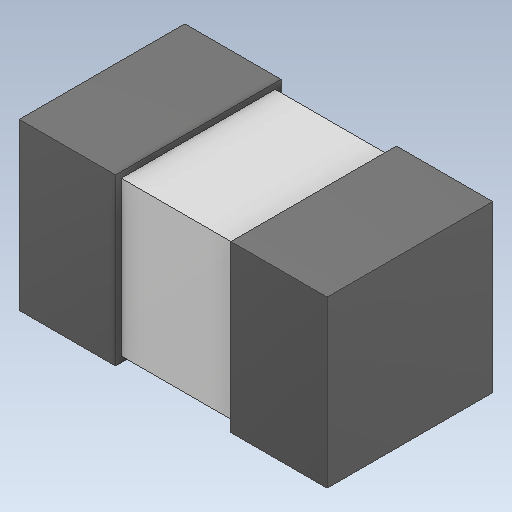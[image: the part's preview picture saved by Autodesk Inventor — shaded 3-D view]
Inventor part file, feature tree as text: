
AUTODESK INVENTOR PART (.ipt)
format: ipt  version: 2020 (Build 240168000, 168)  size: 102,912 bytes
history: native  units: mm
features: other x1, extrude x1
ambient origin geometry x8: Origin, YZ Plane, XZ Plane, XY Plane, X Axis, Y Axis, Z Axis, Center Point
bodies: Body1 (feature_tree)
feature tree (2):
  other  "Твердое тело1"
  extrude  "Extrude2"  [1 undecoded]
note: 1 required parameter value undecoded (feature->parameter linkage not recoverable at this tier; creation-order binding heuristic only, values carry confidence <= 0.55)
